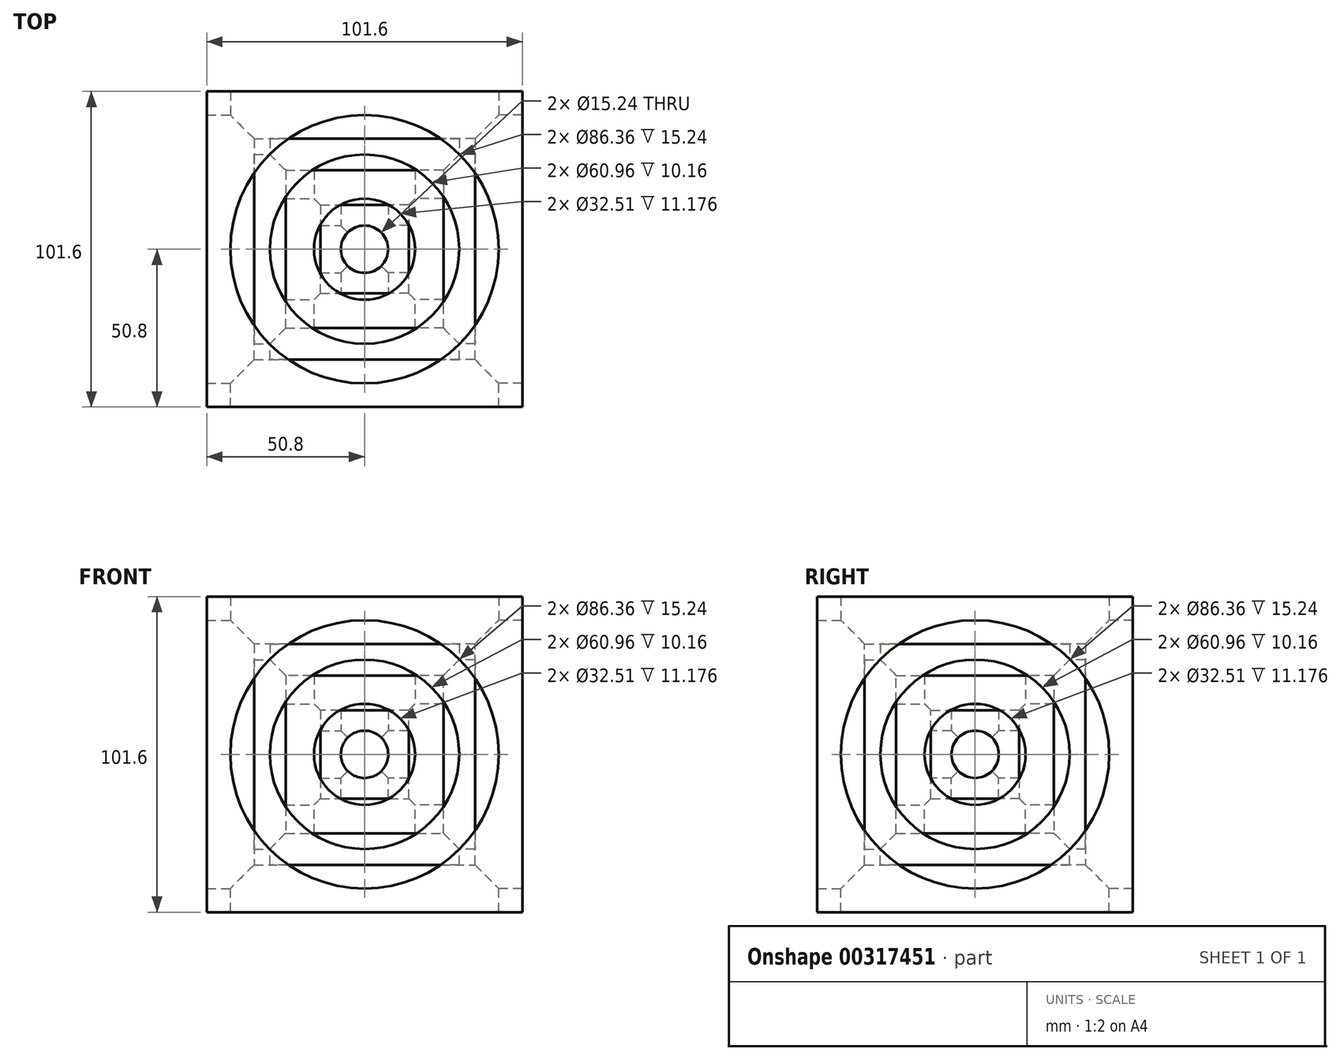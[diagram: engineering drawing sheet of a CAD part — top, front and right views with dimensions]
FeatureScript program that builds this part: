
annotation { "Feature Type Name" : "Feature", "Feature Type Description" : "" }
export const myFeature = defineFeature(function(context is Context, id is Id, definition is map)
    precondition{}
    {
        {
            var Q0;
            Q0=qCreatedBy(makeId("Top.planeOp"),FACE);
            var sketch = newSketch(context, id + "F0", { "sketchPlane" : qUnion([Q0])});
            skLineSegment(sketch, "E0.bottom", {"start": v(-50.8, 50.8) * mm, "end": v(50.8, 50.8) * mm});
            skLineSegment(sketch, "E0.top", {"start": v(-50.8, -50.8) * mm, "end": v(50.8, -50.8) * mm});
            skLineSegment(sketch, "E0.left", {"start": v(-50.8, 50.8) * mm, "end": v(-50.8, -50.8) * mm});
            skLineSegment(sketch, "E0.right", {"start": v(50.8, 50.8) * mm, "end": v(50.8, -50.8) * mm});
            skSolve(sketch);
        }
        {
            var Q0;
            Q0=makeQuery(id+"F0.imprint","IMPRINT",FACE,{"disambiguationData":[TD([[makeQuery(id+"F0.imprint","IMPRINT",EDGE,{"derivedFrom":sQuery(id+"F0.wireOp",EDGE,"E0.bottom")}),-1.0]])]});
            extrude(context, id + "F1", {"entities" : qUnion([Q0]), "depth" : 50.8 * mm, "hasSecondDirection" : true, "secondDirectionOppositeDirection" : true, "secondDirectionDepth" : 50.8 * mm});
        }
        {
            var Q0;
            Q0=qCreatedBy(makeId("Top.planeOp"),FACE);
            var sketch = newSketch(context, id + "F2", { "sketchPlane" : qUnion([Q0])});
            skLineSegment(sketch, "E1", {"start": v(-41.11, 50.8) * mm, "end": v(0, 50.8) * mm});
            skLineSegment(sketch, "E2", {"start": v(0, 50.8) * mm, "end": v(0, 0) * mm});
            skLineSegment(sketch, "E3", {"start": v(0, 0) * mm, "end": v(-7.62, 0) * mm});
            skLineSegment(sketch, "E4", {"start": v(-7.62, 0) * mm, "end": v(-7.62, 14.22) * mm});
            skLineSegment(sketch, "E5", {"start": v(-7.62, 14.22) * mm, "end": v(-16.26, 14.22) * mm});
            skLineSegment(sketch, "E6", {"start": v(-16.26, 14.22) * mm, "end": v(-16.26, 25.4) * mm});
            skLineSegment(sketch, "E7", {"start": v(-16.26, 25.4) * mm, "end": v(-30.48, 25.4) * mm});
            skLineSegment(sketch, "E8", {"start": v(-30.48, 25.4) * mm, "end": v(-30.48, 35.56) * mm});
            skLineSegment(sketch, "E9", {"start": v(-30.48, 35.56) * mm, "end": v(-43.18, 35.56) * mm});
            skLineSegment(sketch, "E10", {"start": v(-43.18, 35.56) * mm, "end": v(-43.18, 50.8) * mm});
            skLineSegment(sketch, "E11", {"start": v(-43.18, 50.8) * mm, "end": v(-41.11, 50.8) * mm});
            skSolve(sketch);
        }
        {
            var Q0;
            Q0=qSketchRegion(id+"F2",true);
            var Q1;
            Q1=sQuery(id+"F2.wireOp",EDGE,"E2");
            revolve(context, id + "F3", {"operationType" : NewBodyOperationType.REMOVE, "entities" : qUnion([Q0]), "axis" : qUnion([Q1]), "revolveType" : RevolveType.FULL, "oppositeDirection" : true});
        }
        {
            var Q0;
            Q0=qCreatedBy(makeId("Top.planeOp"),FACE);
            var sketch = newSketch(context, id + "F4", { "sketchPlane" : qUnion([Q0])});
            skLineSegment(sketch, "E12", {"start": v(13.88, -50.8) * mm, "end": v(0, -50.8) * mm});
            skLineSegment(sketch, "E13", {"start": v(0, -50.8) * mm, "end": v(0, 0) * mm});
            skLineSegment(sketch, "E14", {"start": v(0, 0) * mm, "end": v(7.62, 0) * mm});
            skLineSegment(sketch, "E15", {"start": v(7.62, 0) * mm, "end": v(7.62, -14.22) * mm});
            skLineSegment(sketch, "E16", {"start": v(7.62, -14.22) * mm, "end": v(16.26, -14.22) * mm});
            skLineSegment(sketch, "E17", {"start": v(16.26, -14.22) * mm, "end": v(16.26, -25.4) * mm});
            skLineSegment(sketch, "E18", {"start": v(16.26, -25.4) * mm, "end": v(30.48, -25.4) * mm});
            skLineSegment(sketch, "E19", {"start": v(30.48, -25.4) * mm, "end": v(30.48, -35.56) * mm});
            skLineSegment(sketch, "E20", {"start": v(30.48, -35.56) * mm, "end": v(43.18, -35.56) * mm});
            skLineSegment(sketch, "E21", {"start": v(43.18, -35.56) * mm, "end": v(43.18, -50.8) * mm});
            skLineSegment(sketch, "E22", {"start": v(43.18, -50.8) * mm, "end": v(13.88, -50.8) * mm});
            skSolve(sketch);
        }
        {
            var Q0;
            Q0=qSketchRegion(id+"F4",true);
            var Q1;
            Q1=sQuery(id+"F4.wireOp",EDGE,"E13");
            revolve(context, id + "F5", {"operationType" : NewBodyOperationType.REMOVE, "entities" : qUnion([Q0]), "axis" : qUnion([Q1]), "revolveType" : RevolveType.FULL, "oppositeDirection" : true});
        }
        {
            var Q0;
            Q0=qCreatedBy(makeId("Top.planeOp"),FACE);
            var sketch = newSketch(context, id + "F6", { "sketchPlane" : qUnion([Q0])});
            skLineSegment(sketch, "E23", {"start": v(50.8, 16.38) * mm, "end": v(50.8, 0) * mm});
            skLineSegment(sketch, "E24", {"start": v(50.8, 0) * mm, "end": v(0, 0) * mm});
            skLineSegment(sketch, "E25", {"start": v(0, 0) * mm, "end": v(0, 7.62) * mm});
            skLineSegment(sketch, "E26", {"start": v(0, 7.62) * mm, "end": v(14.22, 7.62) * mm});
            skLineSegment(sketch, "E27", {"start": v(14.22, 7.62) * mm, "end": v(14.22, 16.26) * mm});
            skLineSegment(sketch, "E28", {"start": v(14.22, 16.26) * mm, "end": v(25.4, 16.26) * mm});
            skLineSegment(sketch, "E29", {"start": v(25.4, 16.26) * mm, "end": v(25.4, 30.48) * mm});
            skLineSegment(sketch, "E30", {"start": v(25.4, 30.48) * mm, "end": v(35.56, 30.48) * mm});
            skLineSegment(sketch, "E31", {"start": v(35.56, 30.48) * mm, "end": v(35.56, 43.18) * mm});
            skLineSegment(sketch, "E32", {"start": v(35.56, 43.18) * mm, "end": v(50.8, 43.18) * mm});
            skLineSegment(sketch, "E33", {"start": v(50.8, 43.18) * mm, "end": v(50.8, 16.38) * mm});
            skSolve(sketch);
        }
        {
            var Q0;
            Q0=makeQuery(id+"F6.imprint","IMPRINT",FACE,{"disambiguationData":[TD([[makeQuery(id+"F6.imprint","IMPRINT",EDGE,{"derivedFrom":sQuery(id+"F6.wireOp",EDGE,"E23")}),-1.0]])]});
            var Q1;
            Q1=sQuery(id+"F6.wireOp",EDGE,"E24");
            revolve(context, id + "F7", {"operationType" : NewBodyOperationType.REMOVE, "entities" : qUnion([Q0]), "axis" : qUnion([Q1]), "revolveType" : RevolveType.FULL, "oppositeDirection" : true});
        }
        {
            var Q0;
            Q0=qCreatedBy(makeId("Top.planeOp"),FACE);
            var sketch = newSketch(context, id + "F8", { "sketchPlane" : qUnion([Q0])});
            skLineSegment(sketch, "E34", {"start": v(-50.8, -43.18) * mm, "end": v(-50.8, 0) * mm});
            skLineSegment(sketch, "E35", {"start": v(-50.8, 0) * mm, "end": v(0, 0) * mm});
            skLineSegment(sketch, "E36", {"start": v(0, 0) * mm, "end": v(0, -7.62) * mm});
            skLineSegment(sketch, "E37", {"start": v(0, -7.62) * mm, "end": v(-14.22, -7.62) * mm});
            skLineSegment(sketch, "E38", {"start": v(-14.22, -7.62) * mm, "end": v(-14.22, -16.26) * mm});
            skLineSegment(sketch, "E39", {"start": v(-14.22, -16.26) * mm, "end": v(-25.4, -16.26) * mm});
            skLineSegment(sketch, "E40", {"start": v(-25.4, -16.26) * mm, "end": v(-25.4, -30.48) * mm});
            skLineSegment(sketch, "E41", {"start": v(-25.4, -30.48) * mm, "end": v(-35.56, -30.48) * mm});
            skLineSegment(sketch, "E42", {"start": v(-35.56, -30.48) * mm, "end": v(-35.56, -43.18) * mm});
            skLineSegment(sketch, "E43", {"start": v(-35.56, -43.18) * mm, "end": v(-50.8, -43.18) * mm});
            skSolve(sketch);
        }
        {
            var Q0;
            Q0=qSketchRegion(id+"F8",true);
            var Q1;
            Q1=sQuery(id+"F8.wireOp",EDGE,"E35");
            revolve(context, id + "F9", {"operationType" : NewBodyOperationType.REMOVE, "entities" : qUnion([Q0]), "axis" : qUnion([Q1]), "revolveType" : RevolveType.FULL, "oppositeDirection" : true});
        }
        {
            var Q0;
            Q0=qCreatedBy(makeId("Right.planeOp"),FACE);
            var sketch = newSketch(context, id + "F10", { "sketchPlane" : qUnion([Q0])});
            skLineSegment(sketch, "E44", {"start": v(0, 0) * mm, "end": v(-7.62, 0) * mm});
            skLineSegment(sketch, "E45", {"start": v(-7.62, 0) * mm, "end": v(-7.62, 14.22) * mm});
            skLineSegment(sketch, "E46", {"start": v(-7.62, 14.22) * mm, "end": v(-16.26, 14.22) * mm});
            skLineSegment(sketch, "E47", {"start": v(-16.26, 14.22) * mm, "end": v(-16.26, 25.4) * mm});
            skLineSegment(sketch, "E48", {"start": v(-16.26, 25.4) * mm, "end": v(-30.48, 25.4) * mm});
            skLineSegment(sketch, "E49", {"start": v(-30.48, 25.4) * mm, "end": v(-30.48, 35.56) * mm});
            skLineSegment(sketch, "E50", {"start": v(-30.48, 35.56) * mm, "end": v(-43.18, 35.56) * mm});
            skLineSegment(sketch, "E51", {"start": v(-43.18, 35.56) * mm, "end": v(-43.18, 50.8) * mm});
            skLineSegment(sketch, "E52", {"start": v(-43.18, 50.8) * mm, "end": v(0, 50.8) * mm});
            skLineSegment(sketch, "E53", {"start": v(0, 50.8) * mm, "end": v(0, 0) * mm});
            skSolve(sketch);
        }
        {
            var Q0;
            Q0=qSketchRegion(id+"F10",true);
            var Q1;
            Q1=sQuery(id+"F10.wireOp",EDGE,"E53");
            revolve(context, id + "F11", {"operationType" : NewBodyOperationType.REMOVE, "entities" : qUnion([Q0]), "axis" : qUnion([Q1]), "revolveType" : RevolveType.FULL, "oppositeDirection" : true});
        }
        {
            var Q0;
            Q0=qCreatedBy(makeId("Right.planeOp"),FACE);
            var sketch = newSketch(context, id + "F12", { "sketchPlane" : qUnion([Q0])});
            skLineSegment(sketch, "E54", {"start": v(0, 0) * mm, "end": v(7.62, 0) * mm});
            skLineSegment(sketch, "E55", {"start": v(7.62, 0) * mm, "end": v(7.62, -14.22) * mm});
            skLineSegment(sketch, "E56", {"start": v(7.62, -14.22) * mm, "end": v(16.26, -14.22) * mm});
            skLineSegment(sketch, "E57", {"start": v(16.26, -14.22) * mm, "end": v(16.26, -25.4) * mm});
            skLineSegment(sketch, "E58", {"start": v(16.26, -25.4) * mm, "end": v(30.48, -25.4) * mm});
            skLineSegment(sketch, "E59", {"start": v(30.48, -25.4) * mm, "end": v(30.48, -35.56) * mm});
            skLineSegment(sketch, "E60", {"start": v(30.48, -35.56) * mm, "end": v(43.18, -35.56) * mm});
            skLineSegment(sketch, "E61", {"start": v(43.18, -35.56) * mm, "end": v(43.18, -50.8) * mm});
            skLineSegment(sketch, "E62", {"start": v(43.18, -50.8) * mm, "end": v(0, -50.8) * mm});
            skLineSegment(sketch, "E63", {"start": v(0, -50.8) * mm, "end": v(0, 0) * mm});
            skSolve(sketch);
        }
        {
            var Q0;
            Q0=qSketchRegion(id+"F12",true);
            var Q1;
            Q1=sQuery(id+"F12.wireOp",EDGE,"E63");
            revolve(context, id + "F13", {"operationType" : NewBodyOperationType.REMOVE, "entities" : qUnion([Q0]), "axis" : qUnion([Q1]), "revolveType" : RevolveType.FULL, "oppositeDirection" : true});
        }
    });
